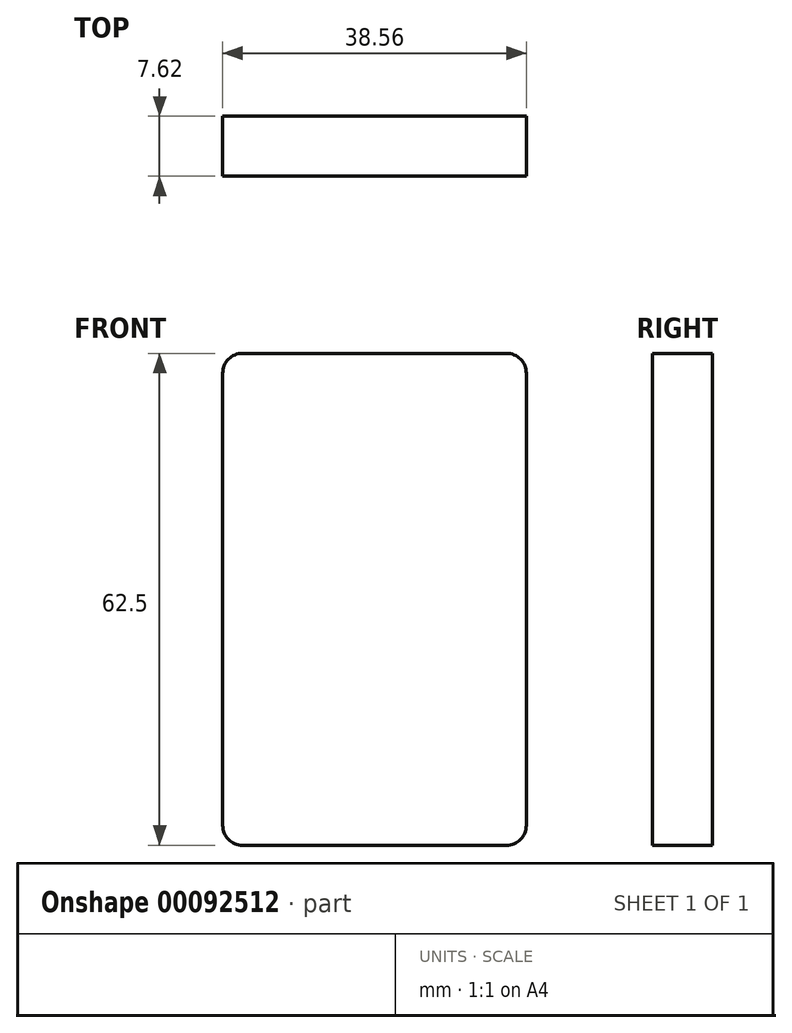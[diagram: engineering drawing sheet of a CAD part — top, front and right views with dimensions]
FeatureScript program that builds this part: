
annotation { "Feature Type Name" : "Feature", "Feature Type Description" : "" }
export const myFeature = defineFeature(function(context is Context, id is Id, definition is map)
    precondition{}
    {
        {
            var Q0;
            Q0=qCreatedBy(makeId("Front.planeOp"),FACE);
            var sketch = newSketch(context, id + "F0", { "sketchPlane" : qUnion([Q0])});
            skLineSegment(sketch, "E0.bottom", {"start": v(19.28, -31.25) * mm, "end": v(-19.28, -31.25) * mm});
            skLineSegment(sketch, "E0.top", {"start": v(19.28, 31.25) * mm, "end": v(-19.28, 31.25) * mm});
            skLineSegment(sketch, "E0.left", {"start": v(19.28, -31.25) * mm, "end": v(19.28, 31.25) * mm});
            skLineSegment(sketch, "E0.right", {"start": v(-19.28, -31.25) * mm, "end": v(-19.28, 31.25) * mm});
            skPoint(sketch, "E0.middle", {"position": v(0, 0) * mm});
            skSolve(sketch);
        }
        {
            var Q0;
            Q0=makeQuery(id+"F0.imprint","IMPRINT",FACE,{"disambiguationData":[TD([[makeQuery(id+"F0.imprint","IMPRINT",EDGE,{"derivedFrom":sQuery(id+"F0.wireOp",EDGE,"E0.bottom")}),-1.0]])]});
            extrude(context, id + "F1", {"entities" : qUnion([Q0]), "depth" : 7.62 * mm});
        }
        {
            var Q0;
            Q0=makeQuery(id+"F1.opExtrude","SWEPT_EDGE",EDGE,{"disambiguationData":[OSD([sQuery(id+"F0.wireOp",EDGE,"E0.top"),sQuery(id+"F0.wireOp",EDGE,"E0.left")])]});
            var Q1;
            Q1=makeQuery(id+"F1.opExtrude","SWEPT_EDGE",EDGE,{"disambiguationData":[OSD([sQuery(id+"F0.wireOp",EDGE,"E0.top"),sQuery(id+"F0.wireOp",EDGE,"E0.right")])]});
            var Q2;
            Q2=makeQuery(id+"F1.opExtrude","SWEPT_EDGE",EDGE,{"disambiguationData":[OSD([sQuery(id+"F0.wireOp",EDGE,"E0.bottom"),sQuery(id+"F0.wireOp",EDGE,"E0.left")])]});
            var Q3;
            Q3=makeQuery(id+"F1.opExtrude","SWEPT_EDGE",EDGE,{"disambiguationData":[OSD([sQuery(id+"F0.wireOp",EDGE,"E0.bottom"),sQuery(id+"F0.wireOp",EDGE,"E0.right")])]});
            fillet(context, id + "F2", {"entities" : qUnion([Q0, Q1, Q2, Q3]), "radius" : 2.54 * mm, "tangentPropagation" : true, "allowEdgeOverflow" : false});
        }
        {
            var Q0;
            Q0=makeQuery(id+"F1.opExtrude","CAP_FACE",FACE,{"disambiguationData":[OSD([sQuery(id+"F0.wireOp",EDGE,"E0.bottom"),sQuery(id+"F0.wireOp",EDGE,"E0.top"),sQuery(id+"F0.wireOp",EDGE,"E0.left"),sQuery(id+"F0.wireOp",EDGE,"E0.right")])],"isStart":false});
            var sketch = newSketch(context, id + "F3", { "sketchPlane" : qUnion([Q0])});
            skLineSegment(sketch, "E1.bottom", {"start": v(16.74, 28.71) * mm, "end": v(-16.74, 28.71) * mm});
            skLineSegment(sketch, "E1.top", {"start": v(16.74, 8.08) * mm, "end": v(-16.74, 8.08) * mm});
            skLineSegment(sketch, "E1.left", {"start": v(16.74, 28.71) * mm, "end": v(16.74, 8.08) * mm});
            skLineSegment(sketch, "E1.right", {"start": v(-16.74, 28.71) * mm, "end": v(-16.74, 8.08) * mm});
            skPoint(sketch, "E1.middle", {"position": v(0, 18.4) * mm});
            skSolve(sketch);
        }
        {
            var Q0;
            Q0 = qSketchRegion(id + "F3", true);
            var Q1;
            Q1=makeQuery(id+"F3.imprint","IMPRINT",FACE,{"disambiguationData":[TD([[makeQuery(id+"F3.imprint","IMPRINT",EDGE,{"derivedFrom":sQuery(id+"F3.wireOp",EDGE,"E1.bottom")}),-1.0]])]});
            extrude(context, id + "F4", {"entities" : qUnion([Q0, Q1]), "operationType" : NewBodyOperationType.ADD, "oppositeDirection" : true, "depth" : 1.27 * mm});
        }
    });
